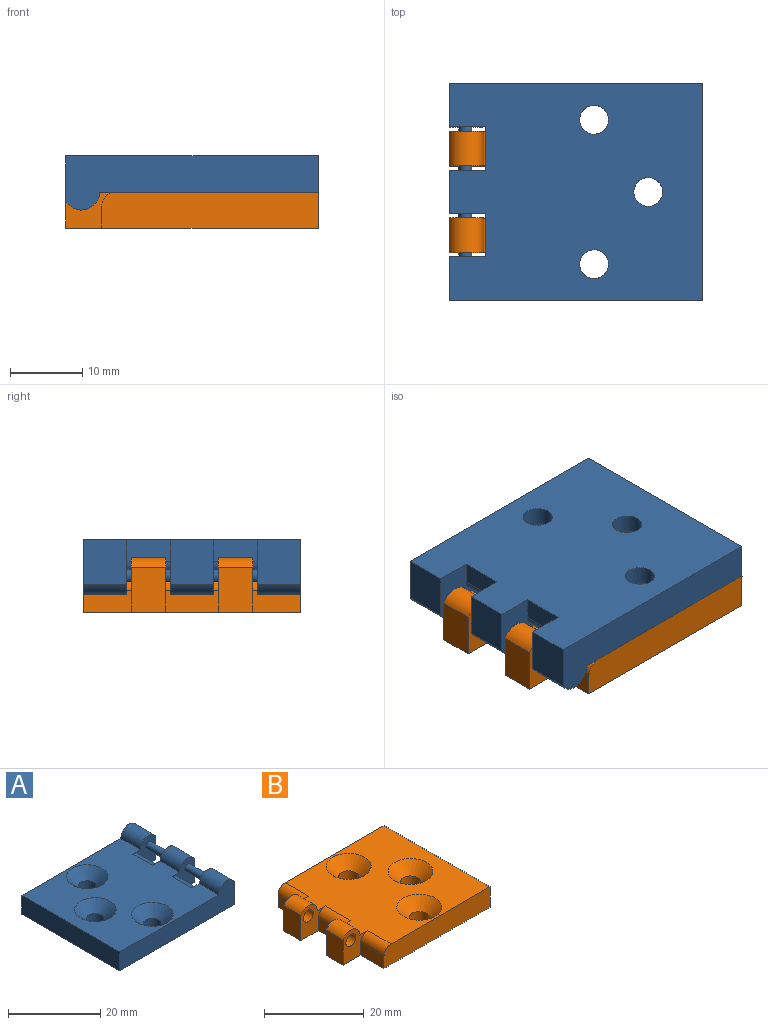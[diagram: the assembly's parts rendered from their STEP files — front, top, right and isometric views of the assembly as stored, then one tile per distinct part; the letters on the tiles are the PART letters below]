
ASSEMBLY  parts=2 mates=1
PART A: 27 faces, bbox 35x30x7.5 mm
  f0: plane 6.19x6mm, normal (1,0,0), area 37.1mm2, adj f4,f7,f8,f10
  f1: cylinder r=2.5mm len=6mm, axis (0,-1,0), area 39.7mm2, adj f6,f9,f11,f19
  f2: cylinder r=2mm len=4mm, axis (0,0,-1), area 31.4mm2, adj f7,f23
  f3: plane 30x5mm, normal (-1,0,0), area 150mm2, adj f4,f6,f7,f15
  f4: plane 35x7.5mm, normal (0,-1,0), area 184.6mm2, adj f0,f3,f6,f7,f8
  f5: cylinder r=2mm len=4mm, axis (0,0,-1), area 31.4mm2, adj f7,f22
  f6: plane 30.3x30mm, normal (0,0,1), area 690.5mm2, adj f1,f3,f4,f8,f10,f11,f15,f17
  f7: plane 35x30mm, normal (0,0,-1), area 952.3mm2, adj f0,f2,f3,f4,f5,f9,f10,f11
  f8: cylinder r=2.5mm len=6mm, axis (0,-1,0), area 39.7mm2, adj f0,f4,f6,f10
  f9: plane 6.19x6mm, normal (1,0,0), area 37.1mm2, adj f1,f7,f11,f19
  f10: plane 7.5x7mm, normal (0,1,0), area 32.9mm2, adj f0,f6,f7,f8,f12,f13,f26
  f11: plane 7.5x7mm, normal (0,-1,0), area 32.9mm2, adj f1,f6,f7,f9,f12,f13,f26
  f12: plane 6x3mm, normal (1,0,0), area 18mm2, adj f7,f10,f11,f26
  f13: cylinder r=0.9mm len=6mm, axis (0,1,0), area 33.9mm2, adj f10,f11
  f14: plane 6.19x6mm, normal (1,0,0), area 37.1mm2, adj f7,f15,f17,f18
  f15: plane 35x7.5mm, normal (0,1,0), area 184.6mm2, adj f3,f6,f7,f14,f17
  f16: cylinder r=2mm len=4mm, axis (0,0,-1), area 31.4mm2, adj f7,f24
  f17: cylinder r=2.5mm len=6mm, axis (0,1,0), area 39.7mm2, adj f6,f14,f15,f18
  f18: plane 7.5x7mm, normal (0,-1,0), area 32.9mm2, adj f6,f7,f14,f17,f20,f21,f25
  f19: plane 7.5x7mm, normal (0,1,0), area 32.9mm2, adj f1,f6,f7,f9,f20,f21,f25
  f20: plane 6x3mm, normal (1,0,0), area 18mm2, adj f7,f18,f19,f25
  f21: cylinder r=0.9mm len=6mm, axis (0,-1,0), area 33.9mm2, adj f18,f19
  f22: cone r=2mm half-angle=45deg, axis (0,0,1), area 72.2mm2, adj f5,f6
  f23: cone r=4.5mm half-angle=45deg, axis (0,0,1), area 72.2mm2, adj f2,f6
  f24: cone r=4.5mm half-angle=45deg, axis (0,0,1), area 72.2mm2, adj f6,f16
  f25: cylinder r=2mm len=6mm, axis (0,-1,0), area 18.8mm2, adj f6,f18,f19,f20
  f26: cylinder r=2mm len=6mm, axis (0,1,0), area 18.8mm2, adj f6,f10,f11,f12
PART B: 27 faces, bbox 35x30x7.5 mm
  f0: plane 7.2x3mm, normal (-1,0,0), area 21.6mm2, adj f7,f11,f19,f26
  f1: cylinder r=2mm len=4mm, axis (0,0,-1), area 31.4mm2, adj f7,f22
  f2: plane 6.6x3mm, normal (-1,0,0), area 19.8mm2, adj f3,f7,f12,f25
  f3: plane 30x5mm, normal (0,-1,0), area 149.1mm2, adj f2,f4,f6,f7,f25
  f4: plane 30x5mm, normal (1,0,0), area 150mm2, adj f3,f6,f7,f14
  f5: cylinder r=2mm len=4mm, axis (0,0,-1), area 31.4mm2, adj f7,f23
  f6: plane 30.3x30mm, normal (0,0,1), area 671.2mm2, adj f3,f4,f9,f11,f12,f14,f17,f19
  f7: plane 35x30mm, normal (0,0,-1), area 910.3mm2, adj f0,f1,f2,f3,f4,f5,f8,f11
  f8: plane 6.19x4.8mm, normal (-1,0,0), area 29.7mm2, adj f7,f9,f11,f12
  f9: cylinder r=2.5mm len=4.8mm, axis (0,-1,0), area 31.8mm2, adj f6,f8,f11,f12
  f10: cylinder r=1.4mm len=4.8mm, axis (0,-1,0), area 42.2mm2, adj f11,f12
  f11: plane 7.5x7mm, normal (0,1,0), area 29.3mm2, adj f0,f6,f7,f8,f9,f10,f26
  f12: plane 7.5x7mm, normal (0,-1,0), area 29.3mm2, adj f2,f6,f7,f8,f9,f10,f25
  f13: plane 6.6x3mm, normal (-1,0,0), area 19.8mm2, adj f7,f14,f20,f24
  f14: plane 30x5mm, normal (0,1,0), area 149.1mm2, adj f4,f6,f7,f13,f24
  f15: cylinder r=2mm len=4mm, axis (0,0,-1), area 31.4mm2, adj f7,f21
  f16: plane 6.19x4.8mm, normal (-1,0,0), area 29.7mm2, adj f7,f17,f19,f20
  f17: cylinder r=2.5mm len=4.8mm, axis (0,1,0), area 31.8mm2, adj f6,f16,f19,f20
  f18: cylinder r=1.4mm len=4.8mm, axis (0,1,0), area 42.2mm2, adj f19,f20
  f19: plane 7.5x7mm, normal (0,-1,0), area 29.3mm2, adj f0,f6,f7,f16,f17,f18,f26
  f20: plane 7.5x7mm, normal (0,1,0), area 29.3mm2, adj f6,f7,f13,f16,f17,f18,f24
  f21: cone r=4.5mm half-angle=45deg, axis (0,0,1), area 72.2mm2, adj f6,f15
  f22: cone r=4.5mm half-angle=45deg, axis (0,0,1), area 72.2mm2, adj f1,f6
  f23: cone r=2mm half-angle=45deg, axis (0,0,1), area 72.2mm2, adj f5,f6
  f24: cylinder r=2mm len=6.6mm, axis (0,-1,0), area 20.7mm2, adj f6,f13,f14,f20
  f25: cylinder r=2mm len=6.6mm, axis (0,1,0), area 20.7mm2, adj f2,f3,f6,f12
  f26: cylinder r=2mm len=7.2mm, axis (0,1,0), area 22.6mm2, adj f0,f6,f11,f19
PLACE A rot(axis=(0,1,0),180deg) t=(7.35,0.39,8.55)mm
PLACE B t=(2.35,0.39,-1.45)mm
MATE revolute A.f1 <-> B.f9  axis (0,1,0) through (4.85,-5.61,3.55)mm
